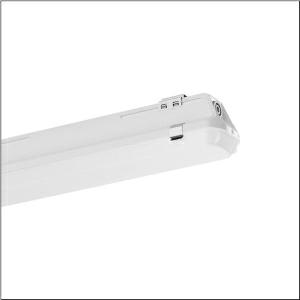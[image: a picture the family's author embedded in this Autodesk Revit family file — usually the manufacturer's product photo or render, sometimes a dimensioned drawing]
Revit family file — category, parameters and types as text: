
# Revit family: monsun_r__21_51fb107l420j005_7c6e
name_source: partatom
category: Lighting Fixtures
units: mm (PartAtom-declared; Revit-internal decimal feet)

## family parameters
Cut with Voids When Loaded = No
Host = Face
Light Source = No
Part Type = Normal
Room Calculation Point = No
Round Connector Dimension = Use Diameter
Shared = No

## types (1)
- Monsun® 21 (1 x LED, 2590 lm, 17.7 W, 4000K)
    Apparent Load = 18 VA
    CIE Flux Codes = 46 76 93 94 100
    Color Rendering = 80
    Color Temperature = 4000K
    Default Elevation = 1800 mm
    Description = Monsun® 21, damp-proof luminaire, chain hanger, primary optical cover: enclosure, of PMMA, light emission: direct distribution, primary light characteristic: symmetric, installation type: vertical mounting, horizontal mounting, surface-mounted, suspended mounting, LED, rated luminous flux: 2.590lm, luminous efficacy: 144lm/W, light colour: 840, colour temperature: 4000K, control gear: ECG, with terminal, 3-pole, max. 2.5mm², through-wiring: 5x 2.5mm², mains connection: 220..240V, AC, 50/60Hz, rated input power: 18W, housing, of glass-fibre reinforced plastic, uncoated, bright grey, incl. chain hanger, length: 1.299mm, width: 90mm, height: 88mm, clip for enclosure, of stainless steel (V2A), ceiling mounting element, of stainless steel (V2A), chain hanger, of stainless steel (V2A), protection rating (complete): IP66, insulation class (complete): insulation class I (protective earthing), certification: CE, ENEC, VDE, UKCA, protection symbol: D, impact resistance: IK04, permissible operating ambient temperature: -25..+35°C, standard: EN 50419, EN 60598-2-1, corresponds to IFS (International Featured Standards) requirements for safety and quality in the food industry, for indoor or canopied outdoor use, no direct snow, no direct sun, no direct rain, contact your sales advisor before using the luminaires in applications with unclear chemical exposure, large temperature fluctuations or condensation-forming humidity, LABS conformity tested according to VDMA 24364:2018-05, packaging unit: 1 piece
    Height = 88 mm
    Lamp = 1 x LED
    Lamp Light Flux = 2590 lm
    Lamp Power = 17.7 W
    Lamp count = 1
    Length = 1299 mm
    Luminous efficacy = 146 lm/W
    Manufacturer = Siteco
    ModVariant = No
    Model = 51FB107L420J005
    Mounting Place = Ceiling
    Mounting Type = Surface mounted
    Number of Poles = 1
    OnlyDefault = Yes
    Power Factor = 1
    Product Name = Monsun® 21
    Product group = damp-proof luminaire
    ProductGroupID = 300
    Protection Class = Protection class I
    Protection Degree = IP 66
    RLX_Detail_Level = 1
    RLX_Emergency_Light_Flux = 0 lm
    RLX_Emergency_Type = 0
    RLX_Emergency_Type_DB = No
    RlxData = <blob elided: 89697 chars, md5=95b45713>
    Socket = socket
    Standby Power = 0 W
    System Light Flux = 2590 lm
    System Power = 18 W
    Type Comments = Product without accessories
    Type Image = l_1006717.jpg
    URL = http://relux.com
    VarID = ---
    Voltage = 0 V
    Weight = 0.00 kg
    Width = 90 mm

## geometry (parser evidence)
native form markers: Blend x4, Sweep x14
no freeform markers — native parametric forms only
